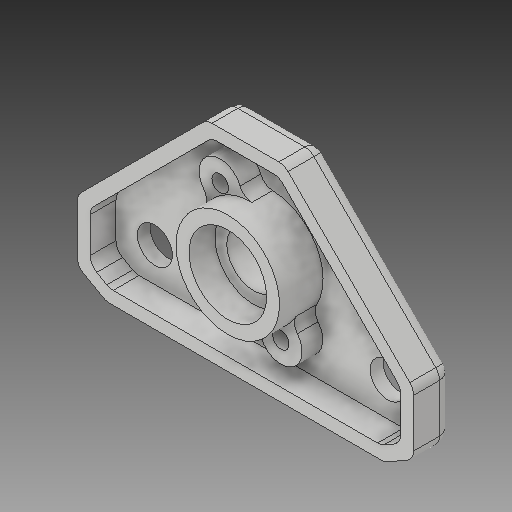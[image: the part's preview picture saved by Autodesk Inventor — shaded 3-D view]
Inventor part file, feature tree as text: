
AUTODESK INVENTOR PART (.ipt)
format: ipt  version: 2017 (Build 210142000, 142)  size: 203,264 bytes
history: native  units: in
note: dims shown in document units (in); Inventor stores cm internally (conversion verified against a paired STEP export)
features: fillet x1
ambient origin geometry x8: Origin, YZ Plane, XZ Plane, XY Plane, X Axis, Y Axis, Z Axis, Center Point
bodies: Solid1 (feature_tree)
feature tree (1):
  fillet  "Fillet2"  [1 undecoded]
note: 1 required parameter value undecoded (feature->parameter linkage not recoverable at this tier; creation-order binding heuristic only, values carry confidence <= 0.55)
